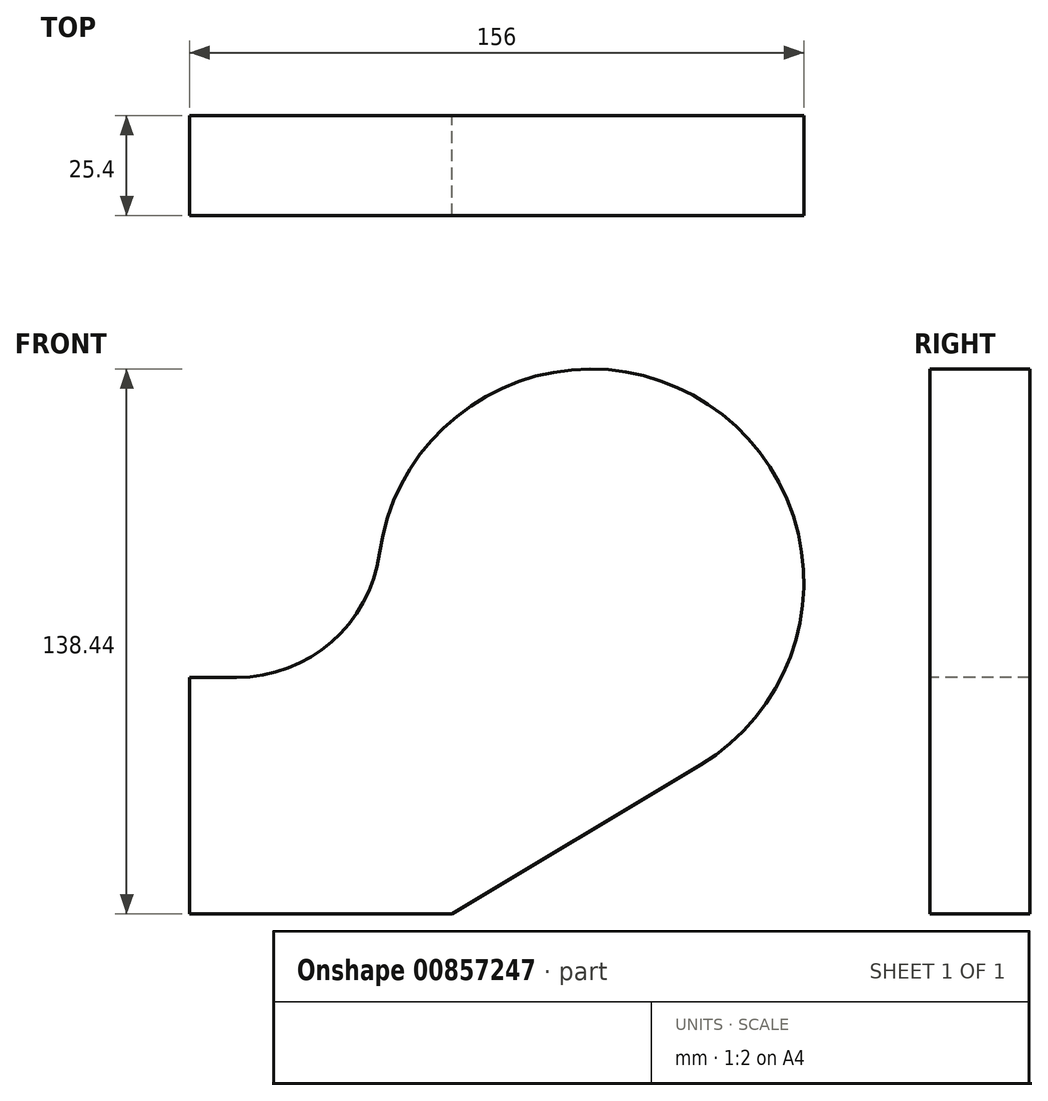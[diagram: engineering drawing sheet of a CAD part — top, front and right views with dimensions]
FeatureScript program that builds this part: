
annotation { "Feature Type Name" : "Feature", "Feature Type Description" : "" }
export const myFeature = defineFeature(function(context is Context, id is Id, definition is map)
    precondition{}
    {
        {
            var Q0;
            Q0=qCreatedBy(makeId("Front.planeOp"),FACE);
            var sketch = newSketch(context, id + "F0", { "sketchPlane" : qUnion([Q0])});
            skCircle(sketch, "E0", {"center": v(0, 0) * mm, "radius": 54.15 * mm});
            skLineSegment(sketch, "E1", {"start": v(-48.43, -24.22) * mm, "end": v(-101.85, -24.22) * mm});
            skLineSegment(sketch, "E2", {"start": v(-101.85, -24.22) * mm, "end": v(-101.85, -84.29) * mm});
            skLineSegment(sketch, "E3", {"start": v(-101.85, -84.29) * mm, "end": v(-35.16, -84.29) * mm});
            skLineSegment(sketch, "E4", {"start": v(-35.16, -84.29) * mm, "end": v(27.88, -46.42) * mm});
            skSolve(sketch);
        }
        {
            var Q0;
            {var subQ0=sQuery(id+"F0.wireOp",EDGE,"E1");Q0=makeQuery(id+"F0.imprint","IMPRINT",FACE,{"disambiguationData":[TD([[makeQuery(id+"F0.imprint","IMPRINT",EDGE,{"derivedFrom":subQ0}),1.0]])]});}
            var Q1;
            {var subQ0=sQuery(id+"F0.wireOp",EDGE,"E0");var subQ1=makeQuery(id+"F0.imprint","INTERSECT",VERTEX,{"derivedFrom":[subQ0,sQuery(id+"F0.wireOp",EDGE,"E1")]});Q1=makeQuery(id+"F0.imprint","IMPRINT",FACE,{"disambiguationData":[TD([[makeQuery(id+"F0.imprint","IMPRINT",EDGE,{"disambiguationData":[TD([[subQ1,-1.0]])],"derivedFrom":subQ0}),1.0]])]});}
            extrude(context, id + "F1", {"entities" : qUnion([Q0, Q1]), "depth" : 25.4 * mm, "offsetDistance" : 25.4 * mm});
        }
        {
            var Q0;
            Q0=makeQuery(id+"F1.opExtrude","SWEPT_EDGE",EDGE,{"disambiguationData":[OSD([sQuery(id+"F0.wireOp",EDGE,"E0"),sQuery(id+"F0.wireOp",EDGE,"E1")])]});
            fillet(context, id + "F2", {"entities" : qUnion([Q0]), "radius" : 36.6 * mm, "tangentPropagation" : true, "allowEdgeOverflow" : false});
        }
    });
